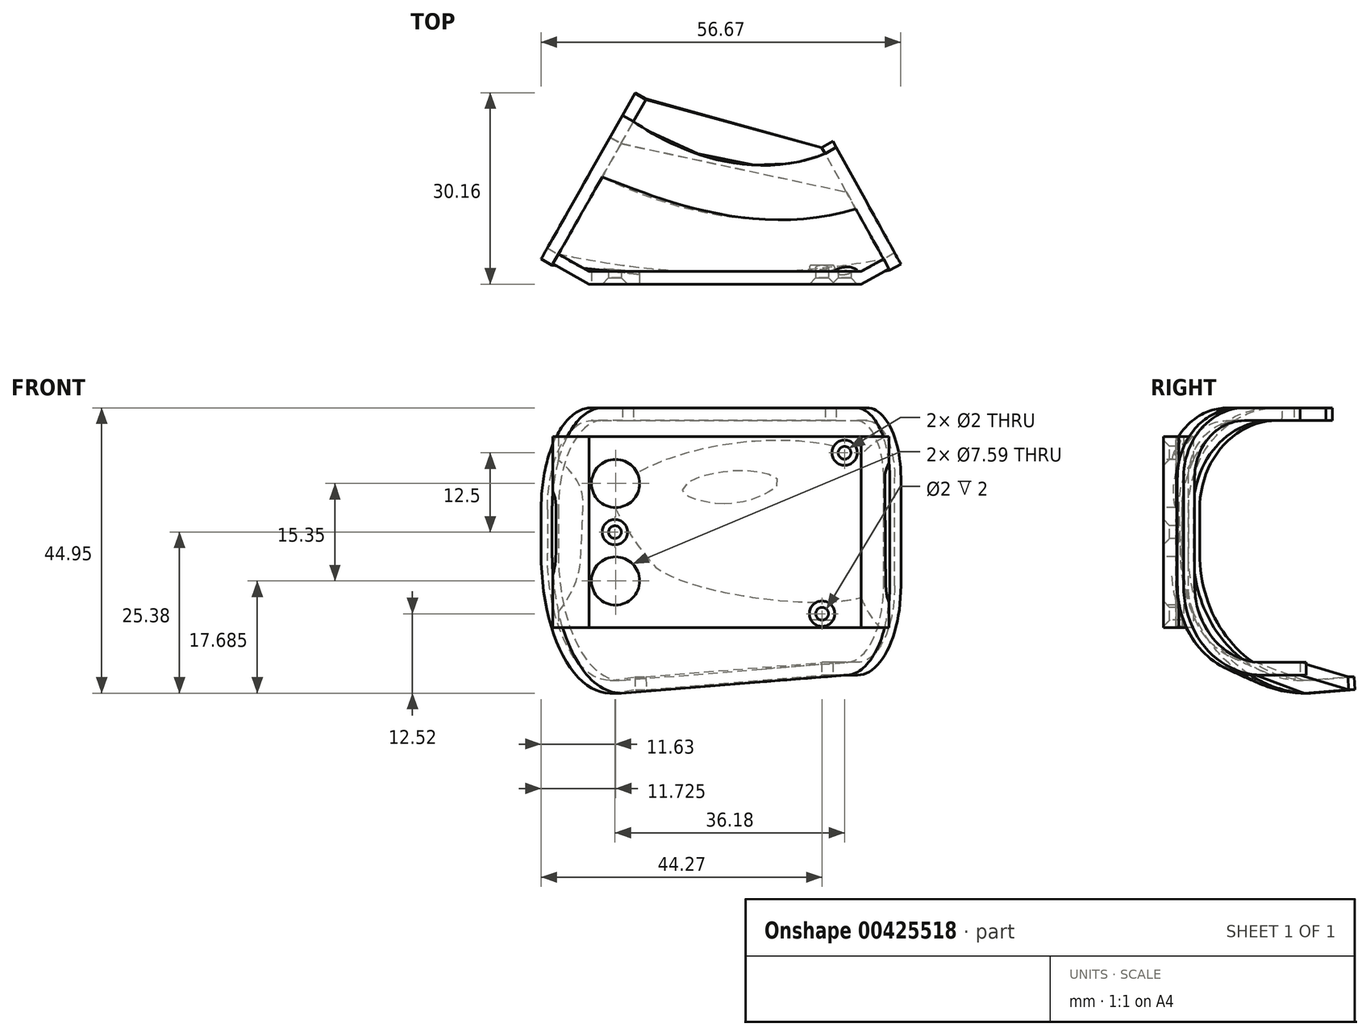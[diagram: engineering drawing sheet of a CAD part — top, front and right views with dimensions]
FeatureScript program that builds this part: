
annotation { "Feature Type Name" : "Feature", "Feature Type Description" : "" }
export const myFeature = defineFeature(function(context is Context, id is Id, definition is map)
    precondition{}
    {
        {
            var Q0;
            Q0=qCreatedBy(makeId("Front.planeOp"),FACE);
            var sketch = newSketch(context, id + "F0", { "sketchPlane" : qUnion([Q0])});
            skLineSegment(sketch, "E0.bottom", {"start": v(21.35, 15.05) * mm, "end": v(-21.35, 15.05) * mm});
            skLineSegment(sketch, "E0.top", {"start": v(21.35, -15.05) * mm, "end": v(-21.35, -15.05) * mm});
            skLineSegment(sketch, "E0.left", {"start": v(21.35, 15.05) * mm, "end": v(21.35, -15.05) * mm});
            skLineSegment(sketch, "E0.right", {"start": v(-21.35, 15.05) * mm, "end": v(-21.35, -15.05) * mm});
            skPoint(sketch, "E0.middle", {"position": v(0, 0) * mm});
            skPoint(sketch, "E1", {"position": v(18.83, 12.5) * mm});
            skPoint(sketch, "E2", {"position": v(15.29, -12.86) * mm});
            skPoint(sketch, "E3", {"position": v(-17.35, 0) * mm});
            skPoint(sketch, "E4", {"position": v(-17.25, 7.66) * mm});
            skPoint(sketch, "E5", {"position": v(-17.25, -7.7) * mm});
            skCircle(sketch, "E6", {"center": v(18.83, 12.5) * mm, "radius": 2 * mm});
            skCircle(sketch, "E7", {"center": v(15.29, -12.86) * mm, "radius": 2 * mm});
            skCircle(sketch, "E8", {"center": v(-17.35, 0) * mm, "radius": 2 * mm});
            skSolve(sketch);
        }
        {
            var Q0;
            Q0=makeQuery(id+"F0.imprint","IMPRINT",FACE,{"disambiguationData":[TD([[makeQuery(id+"F0.imprint","IMPRINT",EDGE,{"derivedFrom":sQuery(id+"F0.wireOp",EDGE,"jPK7hMit-jSFa-N0Mt-JqYe-GtGN3Bu4rccX.bottom")}),1.0]])]});
            var Q1;
            Q1=makeQuery(id+"F0.imprint","IMPRINT",FACE,{"disambiguationData":[TD([[makeQuery(id+"F0.imprint","IMPRINT",EDGE,{"derivedFrom":sQuery(id+"F0.wireOp",EDGE,"E0.bottom")}),1.0]])]});
            var Q2;
            Q2=makeQuery(id+"F0.imprint","IMPRINT",FACE,{"disambiguationData":[TD([[makeQuery(id+"F0.imprint","IMPRINT",EDGE,{"derivedFrom":sQuery(id+"F0.wireOp",EDGE,"e2qhyy3S-mp7l-0j3r-5aax-ppeiUWSRvqxg.bottom")}),1.0]])]});
            var Q3;
            Q3=makeQuery(id+"F0.imprint","IMPRINT",FACE,{"disambiguationData":[TD([[makeQuery(id+"F0.imprint","IMPRINT",EDGE,{"derivedFrom":sQuery(id+"F0.wireOp",EDGE,"aTGAwy4D-jw9e-3WKT-QCMJ-ioXrSI6y0wb3.bottom")}),-1.0]])]});
            var Q4;
            Q4=makeQuery(id+"F0.imprint","IMPRINT",FACE,{"disambiguationData":[TD([[makeQuery(id+"F0.imprint","IMPRINT",EDGE,{"derivedFrom":sQuery(id+"F0.wireOp",EDGE,"E6")}),1.0]])]});
            var Q5;
            Q5=makeQuery(id+"F0.imprint","IMPRINT",FACE,{"disambiguationData":[TD([[makeQuery(id+"F0.imprint","IMPRINT",EDGE,{"derivedFrom":sQuery(id+"F0.wireOp",EDGE,"E8")}),1.0]])]});
            var Q6;
            Q6=makeQuery(id+"F0.imprint","IMPRINT",FACE,{"disambiguationData":[TD([[makeQuery(id+"F0.imprint","IMPRINT",EDGE,{"derivedFrom":sQuery(id+"F0.wireOp",EDGE,"E7")}),1.0]])]});
            extrude(context, id + "F1", {"entities" : qUnion([Q0, Q1, Q2, Q3, Q4, Q5, Q6]), "oppositeDirection" : true, "depth" : 2 * mm});
        }
        {
            var Q0;
            Q0=makeQuery(id+"F0.imprint","IMPRINT",FACE,{"disambiguationData":[TD([[makeQuery(id+"F0.imprint","IMPRINT",EDGE,{"derivedFrom":sQuery(id+"F0.wireOp",EDGE,"E6")}),1.0]])]});
            var Q1;
            Q1=makeQuery(id+"F0.imprint","IMPRINT",FACE,{"disambiguationData":[TD([[makeQuery(id+"F0.imprint","IMPRINT",EDGE,{"derivedFrom":sQuery(id+"F0.wireOp",EDGE,"E7")}),1.0]])]});
            var Q2;
            Q2=makeQuery(id+"F0.imprint","IMPRINT",FACE,{"disambiguationData":[TD([[makeQuery(id+"F0.imprint","IMPRINT",EDGE,{"derivedFrom":sQuery(id+"F0.wireOp",EDGE,"E8")}),1.0]])]});
            extrude(context, id + "F2", {"entities" : qUnion([Q0, Q1, Q2]), "operationType" : NewBodyOperationType.ADD, "oppositeDirection" : true, "depth" : 3 * mm});
        }
        {
            var Q0;
            Q0=makeQuery(id+"F1.opExtrude","SWEPT_FACE",FACE,{"disambiguationData":[OSD([sQuery(id+"F0.wireOp",EDGE,"E0.right")])]});
            extrude(context, id + "F3", {"entities" : qUnion([Q0]), "operationType" : NewBodyOperationType.ADD, "depth" : 0.1 * mm});
        }
        {
            var Q0;
            Q0=makeQuery(id+"F1.opExtrude","SWEPT_FACE",FACE,{"disambiguationData":[OSD([sQuery(id+"F0.wireOp",EDGE,"E0.left")])]});
            extrude(context, id + "F4", {"entities" : qUnion([Q0]), "operationType" : NewBodyOperationType.ADD, "depth" : 0.1 * mm});
        }
        {
            var Q0;
            Q0=makeQuery(id+"F3.opExtrude","CAP_FACE",FACE,{"disambiguationData":[OSD([sQuery(id+"F0.wireOp",EDGE,"E0.right")])],"isStart":false});
            var Q1;
            {var subQ0=sQuery(id+"F0.wireOp",EDGE,"E0.right");Q1=makeQuery(id+"F3.opExtrude","CAP_EDGE",EDGE,{"disambiguationData":[OSD([subQ0]),TDD([makeQuery(id+"F1.opExtrude","CAP_EDGE",EDGE,{"disambiguationData":[OSD([subQ0])],"isStart":true})])],"isStart":false});}
            cPlane(context, id + "F5", {"entities" : qUnion([Q0, Q1]), "cplaneType" : CPlaneType.LINE_ANGLE, "offset" : 25 * mm, "angle" : 29.5 * degree, "width" : 150 * mm, "height" : 150 * mm});
        }
        {
            var Q0;
            Q0=qCreatedBy(id+"F5.planeOp",FACE);
            var sketch = newSketch(context, id + "F6", { "sketchPlane" : qUnion([Q0])});
            skLineSegment(sketch, "E9.bottom", {"start": v(-8.82, 15.05) * mm, "end": v(-10.56, 15.05) * mm});
            skLineSegment(sketch, "E9.top", {"start": v(-8.82, -15.05) * mm, "end": v(-10.56, -15.05) * mm});
            skLineSegment(sketch, "E9.left", {"start": v(-8.82, 15.05) * mm, "end": v(-8.82, -15.05) * mm});
            skLineSegment(sketch, "E9.right", {"start": v(-10.56, 15.05) * mm, "end": v(-10.56, -15.05) * mm});
            skSolve(sketch);
        }
        {
            var Q0;
            Q0=qSketchRegion(id+"F6",true);
            extrude(context, id + "F7", {"entities" : qUnion([Q0]), "operationType" : NewBodyOperationType.ADD, "oppositeDirection" : true, "depth" : 6.5 * mm});
        }
        {
            var Q0;
            Q0=makeQuery(id+"F4.opExtrude","CAP_FACE",FACE,{"disambiguationData":[OSD([sQuery(id+"F0.wireOp",EDGE,"E0.left")])],"isStart":false});
            var Q1;
            {var subQ0=sQuery(id+"F0.wireOp",EDGE,"E0.left");Q1=makeQuery(id+"F4.opExtrude","CAP_EDGE",EDGE,{"disambiguationData":[OSD([subQ0]),TDD([makeQuery(id+"F1.opExtrude","CAP_EDGE",EDGE,{"disambiguationData":[OSD([subQ0])],"isStart":true})])],"isStart":false});}
            cPlane(context, id + "F8", {"entities" : qUnion([Q0, Q1]), "cplaneType" : CPlaneType.LINE_ANGLE, "offset" : 25 * mm, "angle" : 29 * degree, "oppositeDirection" : true, "width" : 150 * mm, "height" : 150 * mm});
        }
        {
            var Q0;
            Q0=qCreatedBy(id+"F8.planeOp",FACE);
            var sketch = newSketch(context, id + "F9", { "sketchPlane" : qUnion([Q0])});
            skLineSegment(sketch, "E10.bottom", {"start": v(10.4, -15.05) * mm, "end": v(8.65, -15.05) * mm});
            skLineSegment(sketch, "E10.top", {"start": v(10.4, 15.05) * mm, "end": v(8.65, 15.05) * mm});
            skLineSegment(sketch, "E10.left", {"start": v(10.4, -15.05) * mm, "end": v(10.4, 15.05) * mm});
            skLineSegment(sketch, "E10.right", {"start": v(8.65, -15.05) * mm, "end": v(8.65, 15.05) * mm});
            skSolve(sketch);
        }
        {
            var Q0;
            Q0=qSketchRegion(id+"F9",true);
            extrude(context, id + "F10", {"entities" : qUnion([Q0]), "operationType" : NewBodyOperationType.ADD, "oppositeDirection" : true, "depth" : 5 * mm});
        }
        {
            var Q0;
            Q0=sQuery(id+"F0.wireOp",VERTEX,"E3");
            var Q1;
            Q1=sQuery(id+"F0.wireOp",VERTEX,"E1");
            var Q2;
            Q2=sQuery(id+"F0.wireOp",VERTEX,"E2");
            var Q3;
            Q3=makeQuery(id+"F1.opExtrude","SWEPT_BODY",BODY,{"disambiguationData":[OSD([sQuery(id+"F0.wireOp",EDGE,"E0.bottom"),sQuery(id+"F0.wireOp",EDGE,"E0.top"),sQuery(id+"F0.wireOp",EDGE,"E0.left"),sQuery(id+"F0.wireOp",EDGE,"E0.right")])]});
            hole(context, id + "F11", {"style" : HoleStyle.C_SINK, "endStyle" : HoleEndStyle.THROUGH, "holeDiameter" : 2 * mm, "cSinkDiameter" : 4 * mm, "cSinkAngle" : 90 * degree, "isTappedThrough" : true, "tappedDepth" : 12 * mm, "tapClearance" : 3, "locations" : qUnion([Q0, Q1, Q2]), "scope" : qUnion([Q3])});
        }
        {
            var Q0;
            Q0=sQuery(id+"F0.wireOp",VERTEX,"E4");
            var Q1;
            Q1=sQuery(id+"F0.wireOp",VERTEX,"E5");
            var Q2;
            Q2=makeQuery(id+"F1.opExtrude","SWEPT_BODY",BODY,{"disambiguationData":[OSD([sQuery(id+"F0.wireOp",EDGE,"E0.bottom"),sQuery(id+"F0.wireOp",EDGE,"E0.top"),sQuery(id+"F0.wireOp",EDGE,"E0.left"),sQuery(id+"F0.wireOp",EDGE,"E0.right")])]});
            hole(context, id + "F12", {"style" : HoleStyle.SIMPLE, "endStyle" : HoleEndStyle.THROUGH, "holeDiameter" : 7.6 * mm, "isTappedThrough" : true, "tappedDepth" : 12 * mm, "tapClearance" : 3, "locations" : qUnion([Q0, Q1]), "scope" : qUnion([Q2])});
        }
        {
            var Q0;
            Q0=makeQuery(id+"F10.opExtrude","CAP_FACE",FACE,{"disambiguationData":[OSD([sQuery(id+"F9.wireOp",EDGE,"E10.bottom"),sQuery(id+"F9.wireOp",EDGE,"E10.top"),sQuery(id+"F9.wireOp",EDGE,"E10.left"),sQuery(id+"F9.wireOp",EDGE,"E10.right")])],"isStart":false});
            var sketch = newSketch(context, id + "F13", { "sketchPlane" : qUnion([Q0])});
            skLineSegment(sketch, "E11", {"start": v(10.35, 17.57) * mm, "end": v(0.35, 17.57) * mm});
            skLineSegment(sketch, "E12", {"start": v(-8.65, 8.57) * mm, "end": v(-8.65, -8.43) * mm});
            skArc(sketch, "E13", {"start": v(0.35, 17.57) * mm, "mid": v(-6.01, 14.93) * mm, "end": v(-8.65, 8.57) * mm});
            skArc(sketch, "E14", {"start": v(-8.65, -8.43) * mm, "mid": v(-5.1, -16.99) * mm, "end": v(3.45, -20.53) * mm});
            skLineSegment(sketch, "E15.1", {"start": v(10.35, 19.57) * mm, "end": v(0.35, 19.57) * mm});
            skArc(sketch, "E15.2", {"start": v(0.35, 19.57) * mm, "mid": v(-7.43, 16.35) * mm, "end": v(-10.65, 8.57) * mm});
            skLineSegment(sketch, "E15.3", {"start": v(-10.65, 8.57) * mm, "end": v(-10.65, -8.43) * mm});
            skArc(sketch, "E15.4", {"start": v(-10.65, -8.43) * mm, "mid": v(-6.52, -18.4) * mm, "end": v(3.45, -22.53) * mm});
            skLineSegment(sketch, "E16", {"start": v(10.35, 19.57) * mm, "end": v(10.35, 17.57) * mm});
            skLineSegment(sketch, "E17", {"start": v(3.45, -20.53) * mm, "end": v(11.45, -20.53) * mm});
            skLineSegment(sketch, "E18", {"start": v(3.45, -22.53) * mm, "end": v(11.45, -22.53) * mm});
            skLineSegment(sketch, "E19", {"start": v(11.45, -20.53) * mm, "end": v(11.45, -22.53) * mm});
            skPoint(sketch, "E20", {"position": v(-8.65, 0.07) * mm});
            skSolve(sketch);
        }
        {
            var Q0;
            Q0=qSketchRegion(id+"F13",true);
            extrude(context, id + "F14", {"entities" : qUnion([Q0]), "operationType" : NewBodyOperationType.ADD, "depth" : 2 * mm});
        }
        {
            var Q0;
            Q0=makeQuery(id+"F7.opExtrude","CAP_FACE",FACE,{"disambiguationData":[OSD([sQuery(id+"F6.wireOp",EDGE,"E9.bottom"),sQuery(id+"F6.wireOp",EDGE,"E9.top"),sQuery(id+"F6.wireOp",EDGE,"E9.left"),sQuery(id+"F6.wireOp",EDGE,"E9.right")])],"isStart":false});
            var sketch = newSketch(context, id + "F15", { "sketchPlane" : qUnion([Q0])});
            skLineSegment(sketch, "E21", {"start": v(8.82, 3.57) * mm, "end": v(8.82, -3.38) * mm});
            skLineSegment(sketch, "E22", {"start": v(-15.18, 17.57) * mm, "end": v(-5.18, 17.57) * mm});
            skLineSegment(sketch, "E23", {"start": v(-11.18, -23.38) * mm, "end": v(-19.16, -22.82) * mm});
            skArc(sketch, "E24", {"start": v(8.82, 3.57) * mm, "mid": v(4.72, 13.47) * mm, "end": v(-5.18, 17.57) * mm});
            skArc(sketch, "E25", {"start": v(-11.18, -23.38) * mm, "mid": v(2.96, -17.52) * mm, "end": v(8.82, -3.38) * mm});
            skLineSegment(sketch, "E26.0", {"start": v(-11.25, -25.38) * mm, "end": v(-19.29, -24.82) * mm});
            skLineSegment(sketch, "E26.1", {"start": v(-15.18, 19.57) * mm, "end": v(-5.18, 19.57) * mm});
            skArc(sketch, "E26.2", {"start": v(10.82, 3.57) * mm, "mid": v(6.14, 14.88) * mm, "end": v(-5.18, 19.57) * mm});
            skLineSegment(sketch, "E26.3", {"start": v(10.82, 3.57) * mm, "end": v(10.82, -3.38) * mm});
            skArc(sketch, "E26.4", {"start": v(-11.25, -25.38) * mm, "mid": v(4.35, -18.96) * mm, "end": v(10.82, -3.38) * mm});
            skLineSegment(sketch, "E27", {"start": v(-15.18, 19.57) * mm, "end": v(-15.18, 17.57) * mm});
            skLineSegment(sketch, "E28", {"start": v(-19.16, -22.82) * mm, "end": v(-19.29, -24.82) * mm});
            skLineSegment(sketch, "E29", {"start": v(-5.18, 17.57) * mm, "end": v(-5.18, -23.38) * mm, "construction": true});
            skSolve(sketch);
        }
        {
            var Q0;
            Q0=qSketchRegion(id+"F15",true);
            extrude(context, id + "F16", {"entities" : qUnion([Q0]), "operationType" : NewBodyOperationType.ADD, "depth" : 2 * mm});
        }
        {
            var Q0;
            Q0=makeQuery(id+"F14.opExtrude","SWEPT_FACE",FACE,{"disambiguationData":[OSD([sQuery(id+"F13.wireOp",EDGE,"E15.1")])]});
            var sketch = newSketch(context, id + "F17", { "sketchPlane" : qUnion([Q0])});
            skFitSpline(sketch, "E30", {"points": [v(-14.43, 25.6) * mm, v(15.76, 20.57) * mm], "startDerivative": vector(15.07, -10.15) * mm, "endDerivative": vector(38.6, 15.56) * mm});
            skSolve(sketch);
        }
        {
            var Q0;
            Q0=makeQuery(id+"F14.opExtrude","SWEPT_FACE",FACE,{"disambiguationData":[OSD([sQuery(id+"F13.wireOp",EDGE,"E11")])]});
            var sketch = newSketch(context, id + "F18", { "sketchPlane" : qUnion([Q0])});
            skFitSpline(sketch, "E31", {"points": [v(15.76, -20.57) * mm, v(-14.43, -25.6) * mm], "startDerivative": vector(-23.57, 9.94) * mm, "endDerivative": vector(-34.7, -22.97) * mm});
            skSolve(sketch);
        }
        {
            var Q0;
            Q0=qSketchRegion(id+"F15",true);
            var Q1;
            Q1=qSketchRegion(id+"F13",true);
            var Q2;
            Q2=sQuery(id+"F17.wireOp",EDGE,"E30");
            var Q3;
            Q3=sQuery(id+"F18.wireOp",EDGE,"E31");
            loft(context, id + "F19", {"operationType" : NewBodyOperationType.ADD, "addGuides" : true, "sheetProfilesArray" : [{ "sheetProfileEntities" : qUnion([Q0]) }, { "sheetProfileEntities" : qUnion([Q1]) }], "guidesArray" : [{ "guideEntities" : qUnion([Q2]), "guideDerivativeType" : LoftGuideDerivativeType.DEFAULT, "guideDerivativeMagnitude" : 1 }, { "guideEntities" : qUnion([Q3]), "guideDerivativeType" : LoftGuideDerivativeType.DEFAULT, "guideDerivativeMagnitude" : 1 }]});
        }
    });
